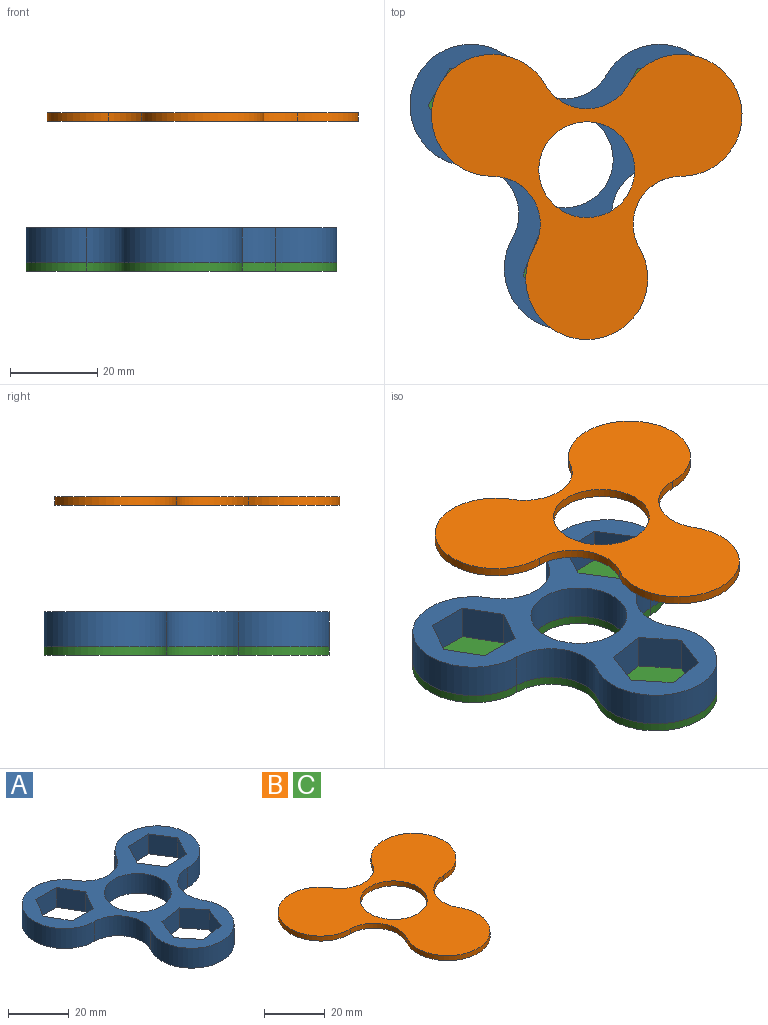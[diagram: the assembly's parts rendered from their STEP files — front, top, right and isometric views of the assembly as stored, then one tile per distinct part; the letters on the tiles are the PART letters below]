
ASSEMBLY  parts=3 mates=1
PART A: 27 faces, bbox 71.3x65.5x8 mm
  f0: plane 9.82x8mm, normal (0,-1,0), area 78.5mm2, adj f1,f24,f25,f26
  f1: plane 8.5x8mm, normal (-0.87,-0.5,0), area 78.5mm2, adj f0,f2,f25,f26
  f2: plane 8.5x8mm, normal (-0.87,0.5,0), area 78.5mm2, adj f1,f3,f25,f26
  f3: plane 9.82x8mm, normal (0,1,0), area 78.5mm2, adj f2,f4,f25,f26
  f4: plane 8.5x8mm, normal (0.87,0.5,0), area 78.5mm2, adj f3,f24,f25,f26
  f5: plane 9.7x8mm, normal (0.15,-0.99,0), area 78.5mm2, adj f6,f20,f25,f26
  f6: plane 8x7.66mm, normal (-0.78,-0.62,0), area 78.5mm2, adj f5,f7,f25,f26
  f7: plane 9.14x8mm, normal (-0.93,0.36,0), area 78.5mm2, adj f6,f8,f25,f26
  f8: plane 9.7x8mm, normal (-0.15,0.99,0), area 78.5mm2, adj f7,f9,f25,f26
  f9: plane 8x7.66mm, normal (0.78,0.62,0), area 78.5mm2, adj f8,f20,f25,f26
  f10: plane 8.67x8mm, normal (0.88,-0.47,0), area 78.5mm2, adj f11,f21,f25,f26
  f11: plane 9.81x8mm, normal (0.04,-1,0), area 78.5mm2, adj f10,f12,f25,f26
  f12: plane 8.31x8mm, normal (-0.85,-0.53,0), area 78.5mm2, adj f11,f13,f25,f26
  f13: plane 8.67x8mm, normal (-0.88,0.47,0), area 78.5mm2, adj f12,f14,f25,f26
  f14: plane 9.81x8mm, normal (-0.04,1,0), area 78.5mm2, adj f13,f21,f25,f26
  f15: cylinder r=11mm len=16.5mm, axis (0,0,-1), area 184.3mm2, adj f16,f22,f25,f26
  f16: cylinder r=14mm len=28mm, axis (0,0,-1), area 469.1mm2, adj f15,f17,f25,f26
  f17: cylinder r=11mm len=16.5mm, axis (0,0,-1), area 184.3mm2, adj f16,f18,f25,f26
  f18: cylinder r=14mm len=28mm, axis (0,0,-1), area 469.1mm2, adj f17,f19,f25,f26
  f19: cylinder r=11mm len=19.05mm, axis (0,0,-1), area 184.3mm2, adj f18,f22,f25,f26
  f20: plane 9.14x8mm, normal (0.93,-0.36,0), area 78.5mm2, adj f5,f9,f25,f26
  f21: plane 8.31x8mm, normal (0.85,0.53,0), area 78.5mm2, adj f10,f14,f25,f26
  f22: cylinder r=14mm len=28mm, axis (0,0,-1), area 469.1mm2, adj f15,f19,f25,f26
  f23: cylinder r=11mm len=22mm, axis (0,0,-1), area 552.9mm2, adj f25,f26
  f24: plane 8.5x8mm, normal (0.87,-0.5,0), area 78.5mm2, adj f0,f4,f25,f26
  f25: plane 71.3x65.5mm, normal (0,0,1), area 1344.2mm2, adj f0,f1,f2,f3,f4,f5,f6,f7
  f26: plane 71.3x65.5mm, normal (0,0,-1), area 1344.2mm2, adj f0,f1,f2,f3,f4,f5,f6,f7
PART B: 9 faces, bbox 71.3x65.5x2 mm
  f0: cylinder r=11mm len=16.5mm, axis (0,0,-1), area 46.1mm2, adj f1,f6,f7,f8
  f1: cylinder r=14mm len=28mm, axis (0,0,-1), area 117.3mm2, adj f0,f2,f7,f8
  f2: cylinder r=11mm len=16.5mm, axis (0,0,-1), area 46.1mm2, adj f1,f3,f7,f8
  f3: cylinder r=14mm len=28mm, axis (0,0,-1), area 117.3mm2, adj f2,f4,f7,f8
  f4: cylinder r=11mm len=19.05mm, axis (0,0,-1), area 46.1mm2, adj f3,f6,f7,f8
  f5: cylinder r=11mm len=22mm, axis (0,0,-1), area 138.2mm2, adj f7,f8
  f6: cylinder r=14mm len=28mm, axis (0,0,-1), area 117.3mm2, adj f0,f4,f7,f8
  f7: plane 71.3x65.5mm, normal (0,0,1), area 2095mm2, adj f0,f1,f2,f3,f4,f5,f6
  f8: plane 71.3x65.5mm, normal (0,0,-1), area 2095mm2, adj f0,f1,f2,f3,f4,f5,f6
PART C: same geometry as B
PLACE A t=(-0.63,-18.18,28.04)mm
PLACE B t=(4.3,-20.53,60.46)mm
PLACE C t=(-0.63,-18.18,26.04)mm
MATE revolute A.f23 <-> C.f5  axis (0,0,-1) through (-0.63,-18.18,28.04)mm
